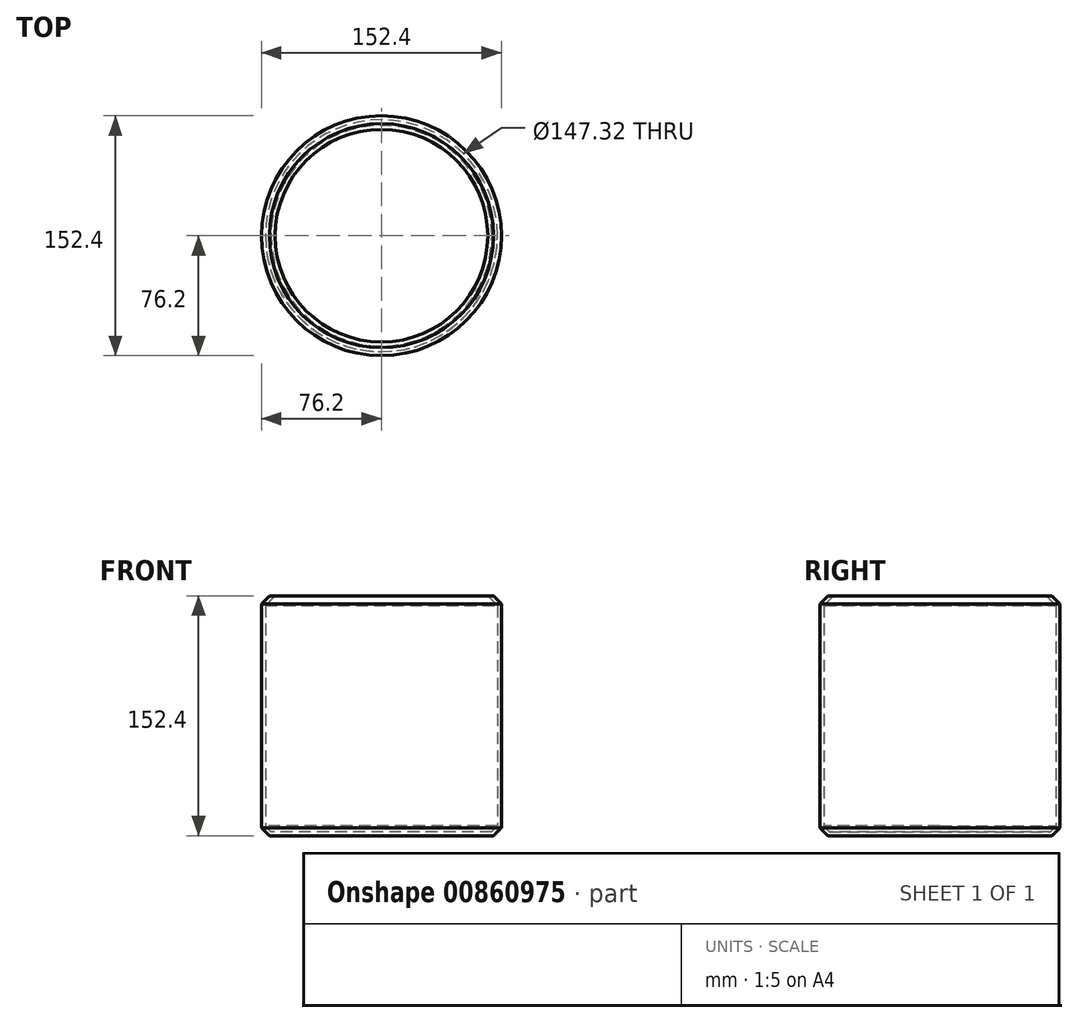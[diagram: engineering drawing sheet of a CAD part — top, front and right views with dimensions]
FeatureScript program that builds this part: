
annotation { "Feature Type Name" : "Feature", "Feature Type Description" : "" }
export const myFeature = defineFeature(function(context is Context, id is Id, definition is map)
    precondition{}
    {
        {
            var Q0;
            Q0=qCreatedBy(makeId("Top.planeOp"),FACE);
            var sketch = newSketch(context, id + "F0", { "sketchPlane" : qUnion([Q0])});
            skCircle(sketch, "E0", {"center": v(0, 0) * mm, "radius": 76.2 * mm});
            skSolve(sketch);
        }
        {
            var Q0;
            Q0=makeQuery(id+"F0.imprint","IMPRINT",FACE,{"disambiguationData":[TD([[makeQuery(id+"F0.imprint","IMPRINT",EDGE,{"derivedFrom":sQuery(id+"F0.wireOp",EDGE,"E0")}),1.0]])]});
            extrude(context, id + "F1", {"entities" : qUnion([Q0]), "depth" : 152.4 * mm, "offsetDistance" : 25.4 * mm});
        }
        {
            var Q0;
            Q0=makeQuery(id+"F1.opExtrude","CAP_FACE",FACE,{"disambiguationData":[OSD([sQuery(id+"F0.wireOp",EDGE,"E0")])],"isStart":false});
            var Q1;
            Q1=makeQuery(id+"F1.opExtrude","SWEPT_FACE",FACE,{"disambiguationData":[OSD([sQuery(id+"F0.wireOp",EDGE,"E0")])]});
            chamfer(context, id + "F2", {"entities" : qUnion([Q0, Q1]), "width" : 5.08 * mm, "tangentPropagation" : true});
        }
        {
            var Q0;
            Q0=makeQuery(id+"F1.opExtrude","CAP_FACE",FACE,{"disambiguationData":[OSD([sQuery(id+"F0.wireOp",EDGE,"E0")])],"isStart":false});
            shell(context, id + "F3", {"entities" : qUnion([Q0]), "thickness" : 2.54 * mm});
        }
    });
